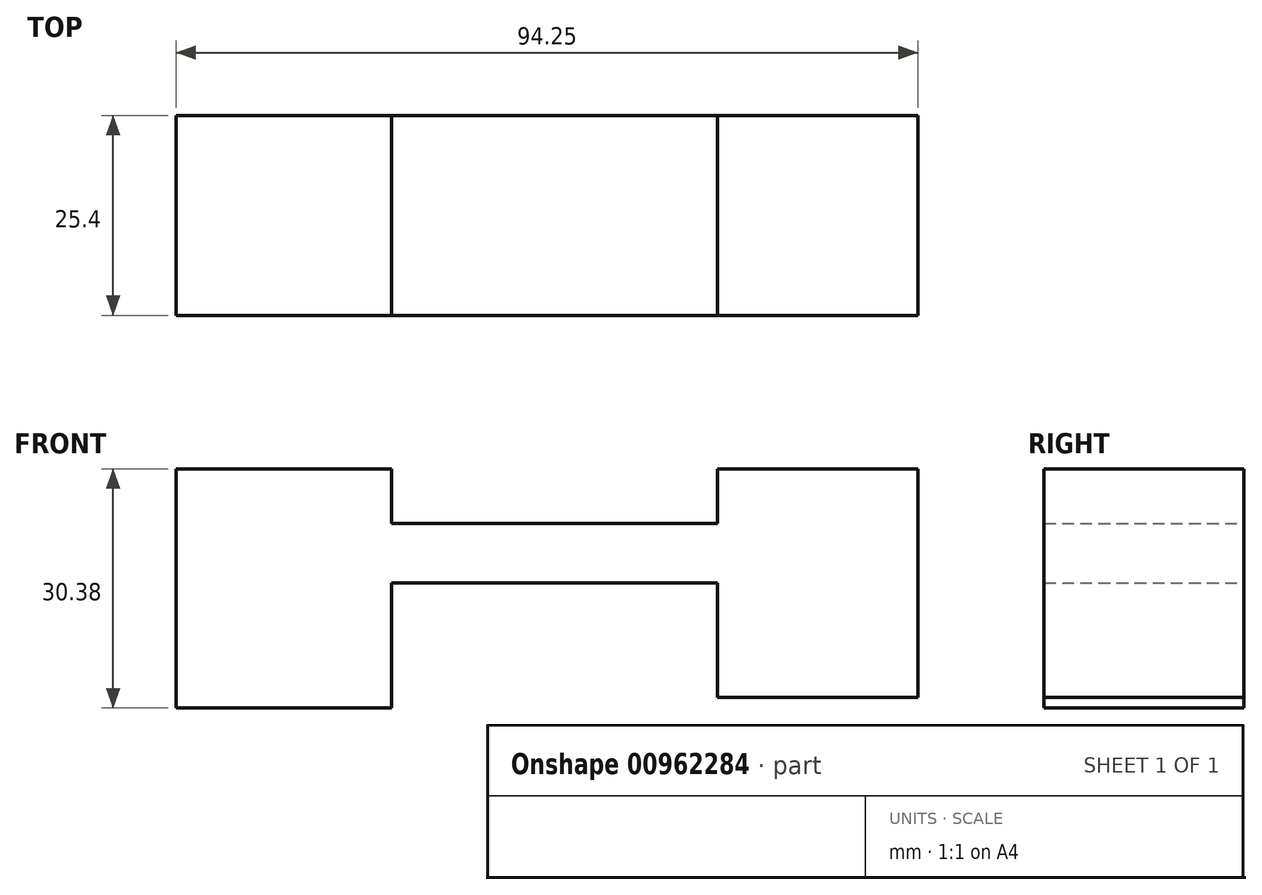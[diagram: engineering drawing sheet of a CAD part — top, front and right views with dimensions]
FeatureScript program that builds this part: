
annotation { "Feature Type Name" : "Feature", "Feature Type Description" : "" }
export const myFeature = defineFeature(function(context is Context, id is Id, definition is map)
    precondition{}
    {
        {
            var Q0;
            Q0=qCreatedBy(makeId("Front.planeOp"),FACE);
            var sketch = newSketch(context, id + "F0", { "sketchPlane" : qUnion([Q0])});
            skLineSegment(sketch, "E0.bottom", {"start": v(49.98, 0) * mm, "end": v(24.5, 0) * mm});
            skLineSegment(sketch, "E0.top", {"start": v(49.98, -29.01) * mm, "end": v(24.5, -29.01) * mm});
            skLineSegment(sketch, "E0.left", {"start": v(49.98, 0) * mm, "end": v(49.98, -29.01) * mm});
            skLineSegment(sketch, "E0.right", {"start": v(24.5, 0) * mm, "end": v(24.5, -29.01) * mm});
            skLineSegment(sketch, "E1.bottom", {"start": v(-44.27, 0) * mm, "end": v(-16.9, 0) * mm});
            skLineSegment(sketch, "E1.top", {"start": v(-44.27, -30.38) * mm, "end": v(-16.9, -30.38) * mm});
            skLineSegment(sketch, "E1.left", {"start": v(-44.27, 0) * mm, "end": v(-44.27, -30.38) * mm});
            skLineSegment(sketch, "E1.right", {"start": v(-16.9, 0) * mm, "end": v(-16.9, -30.38) * mm});
            skLineSegment(sketch, "E2.bottom", {"start": v(-16.9, -6.95) * mm, "end": v(24.5, -6.95) * mm});
            skLineSegment(sketch, "E2.top", {"start": v(-16.9, -14.5) * mm, "end": v(24.5, -14.5) * mm});
            skLineSegment(sketch, "E2.left", {"start": v(-16.9, -6.95) * mm, "end": v(-16.9, -14.5) * mm});
            skLineSegment(sketch, "E2.right", {"start": v(24.5, -6.95) * mm, "end": v(24.5, -14.5) * mm});
            skSolve(sketch);
        }
        {
            var Q0;
            Q0 = qSketchRegion(id + "F0", true);
            extrude(context, id + "F1", {"entities" : qUnion([Q0]), "depth" : 25.4 * mm, "offsetDistance" : 25.4 * mm});
        }
    });
